# Revit family: 251280 Delta kontrollpanel m-eBus
name_source: partatom
category: Electrical Equipment
revit_build: Autodesk Revit 2016 (Build: 20160314_0715(x64)
units: mm (PartAtom-declared; Revit-internal decimal feet)

## family parameters
Always vertical = Yes
Cut with Voids When Loaded = No
OmniClass Number = 23.85.30.21.11
OmniClass Title = Fire Detection, Monitoring and Alarm
Part Type = Other Panel
Room Calculation Point = No
Round Connector Dimension = Use Diameter
Shared = No
Work Plane-Based = No

## types (1)
- Betjeningsenhet
    Assembly Code = 5422
    CQ Depth = 71 mm  [stored 0.23294 ft]
    CQ Display = Laminate, Green
    CQ Font = 0 mm  [stored 0 ft]
    CQ Height = 210 mm  [stored 0.688976 ft]
    CQ Material = Laminate, Grey
    CQ Type = NL
    CQ Type tekst synlig = Yes
    CQ Voltage = 230 V
    CQ Width = 300 mm  [stored 0.984252 ft]
    CQFontSymboler = t
    Keynote = XN5
    Manufacturer = Honeywell
    NS8360 = 5422_XN5
    Type Comments = -OS

note: [stored X ft] marks values corroborated as IEEE doubles in the binary element streams (Revit-internal decimal feet)

## geometry (parser evidence)
native form markers: Blend x2, Sweep x3
no freeform markers — native parametric forms only
